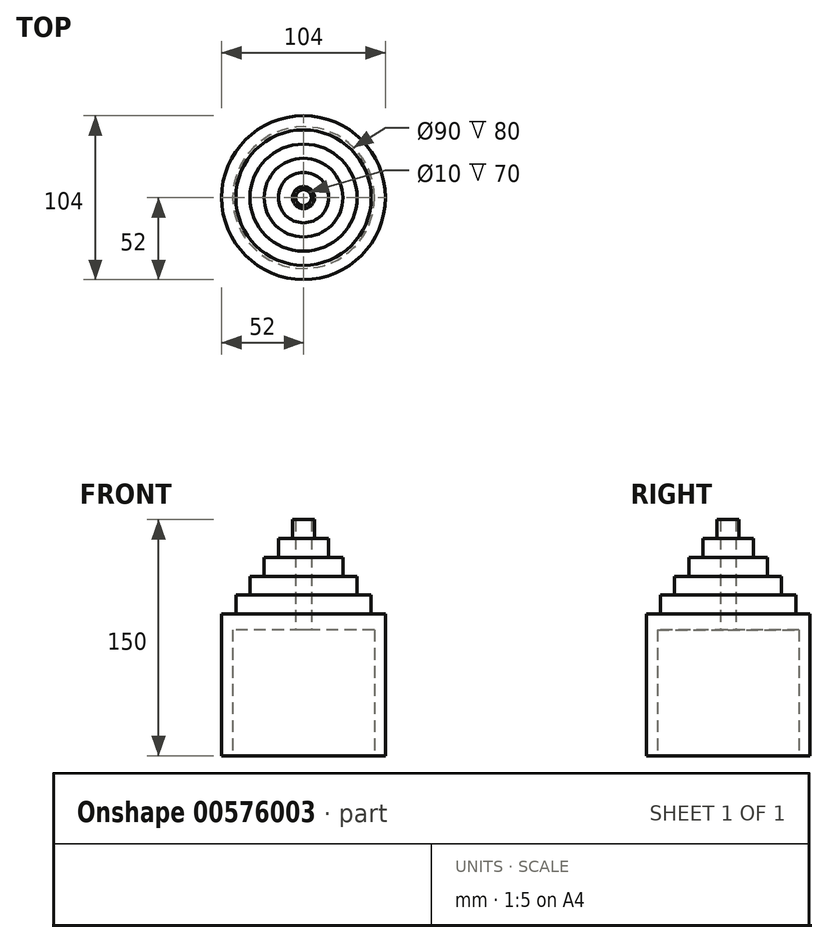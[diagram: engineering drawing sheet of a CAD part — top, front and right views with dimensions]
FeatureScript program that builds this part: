
annotation { "Feature Type Name" : "Feature", "Feature Type Description" : "" }
export const myFeature = defineFeature(function(context is Context, id is Id, definition is map)
    precondition{}
    {
        {
            var Q0;
            Q0=qCreatedBy(makeId("Front.planeOp"),FACE);
            var sketch = newSketch(context, id + "F0", { "sketchPlane" : qUnion([Q0])});
            skLineSegment(sketch, "E0.bottom", {"start": v(0, 0) * mm, "end": v(-52, 0) * mm});
            skLineSegment(sketch, "E0.top", {"start": v(0, 150) * mm, "end": v(-2, 150) * mm});
            skLineSegment(sketch, "E0.left", {"start": v(0, 0) * mm, "end": v(0, 150) * mm});
            skLineSegment(sketch, "E1", {"start": v(-52, 90) * mm, "end": v(-43, 90) * mm});
            skLineSegment(sketch, "E2", {"start": v(-43, 90) * mm, "end": v(-43, 102) * mm});
            skLineSegment(sketch, "E3", {"start": v(-43, 102) * mm, "end": v(-34, 102) * mm});
            skLineSegment(sketch, "E4", {"start": v(-34, 102) * mm, "end": v(-34, 114) * mm});
            skLineSegment(sketch, "E5", {"start": v(-34, 114) * mm, "end": v(-25, 114) * mm});
            skLineSegment(sketch, "E6", {"start": v(-25, 114) * mm, "end": v(-25, 126) * mm});
            skLineSegment(sketch, "E7", {"start": v(-25, 126) * mm, "end": v(-16, 126) * mm});
            skLineSegment(sketch, "E8", {"start": v(-16, 126) * mm, "end": v(-16, 138) * mm});
            skLineSegment(sketch, "E9", {"start": v(-16, 138) * mm, "end": v(-7, 138) * mm});
            skLineSegment(sketch, "E10", {"start": v(-7, 138) * mm, "end": v(-7, 150) * mm});
            skLineSegment(sketch, "E11", {"start": v(-7, 150) * mm, "end": v(0, 150) * mm});
            skLineSegment(sketch, "E12", {"start": v(-52, 90) * mm, "end": v(-52, 0) * mm});
            skSolve(sketch);
        }
        {
            var Q0;
            Q0=qSketchRegion(id+"F0",true);
            var Q1;
            Q1=sQuery(id+"F0.wireOp",EDGE,"E0.left");
            revolve(context, id + "F1", {"entities" : qUnion([Q0]), "axis" : qUnion([Q1]), "revolveType" : RevolveType.FULL});
        }
        {
            var Q0;
            Q0=qCreatedBy(makeId("Top.planeOp"),FACE);
            var sketch = newSketch(context, id + "F2", { "sketchPlane" : qUnion([Q0])});
            skCircle(sketch, "E13", {"center": v(0, 0) * mm, "radius": 45 * mm});
            skSolve(sketch);
        }
        {
            var Q0;
            Q0=qSketchRegion(id+"F2",true);
            extrude(context, id + "F3", {"entities" : qUnion([Q0]), "operationType" : NewBodyOperationType.REMOVE, "depth" : 80 * mm, "offsetDistance" : 25 * mm});
        }
        {
            var Q0;
            Q0=qCreatedBy(makeId("Top.planeOp"),FACE);
            var sketch = newSketch(context, id + "F4", { "sketchPlane" : qUnion([Q0])});
            skCircle(sketch, "E14", {"center": v(0, 0) * mm, "radius": 5 * mm});
            skSolve(sketch);
        }
        {
            var Q0;
            Q0=qSketchRegion(id+"F4",true);
            extrude(context, id + "F5", {"entities" : qUnion([Q0]), "operationType" : NewBodyOperationType.REMOVE, "endBound" : BoundingType.THROUGH_ALL, "depth" : 25 * mm, "offsetDistance" : 25 * mm});
        }
    });
